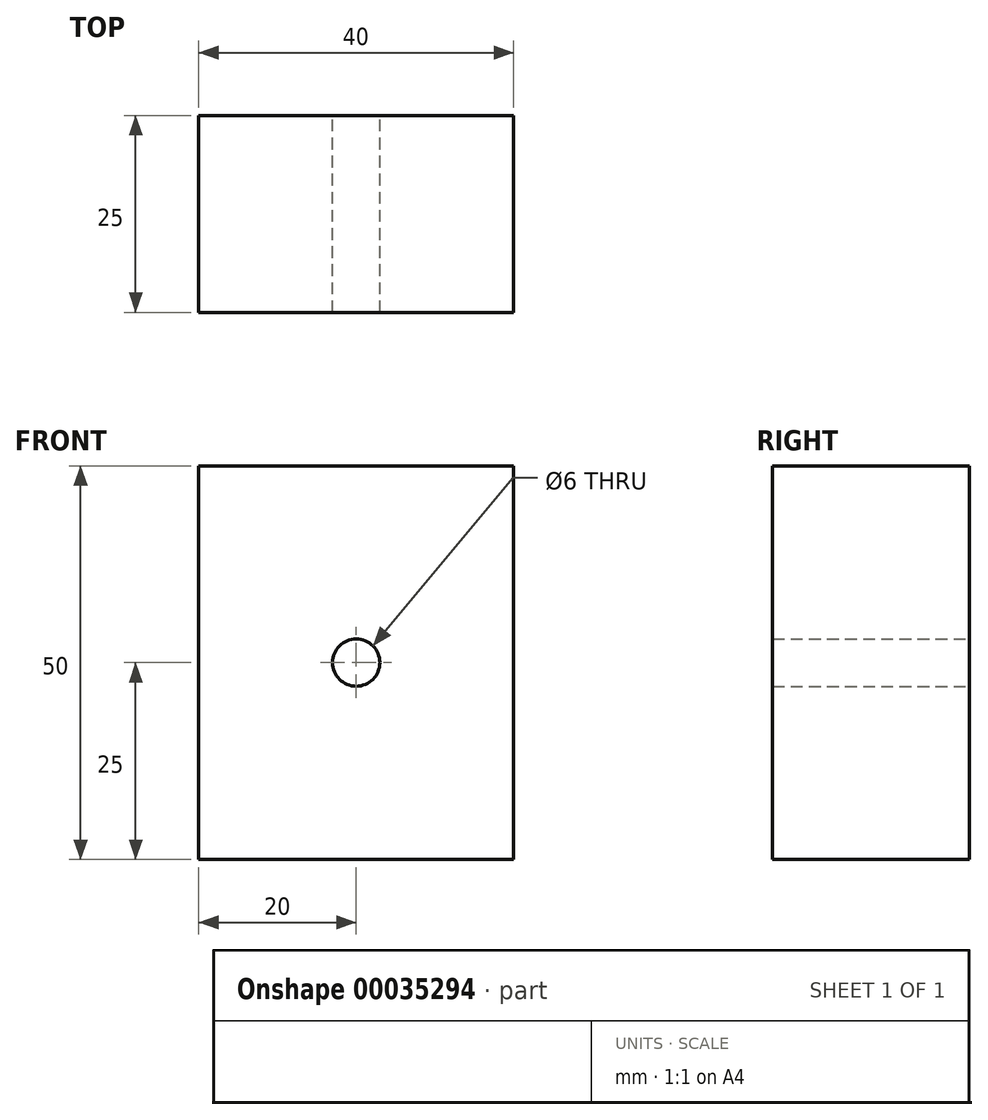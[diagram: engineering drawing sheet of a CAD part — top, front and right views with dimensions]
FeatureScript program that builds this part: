
annotation { "Feature Type Name" : "Feature", "Feature Type Description" : "" }
export const myFeature = defineFeature(function(context is Context, id is Id, definition is map)
    precondition{}
    {
        {
            var Q0;
            Q0=qCreatedBy(makeId("Front.planeOp"),FACE);
            var sketch = newSketch(context, id + "F0", { "sketchPlane" : qUnion([Q0])});
            skCircle(sketch, "E0", {"center": v(0, 0) * mm, "radius": 3 * mm});
            skLineSegment(sketch, "E1.bottom", {"start": v(-20, 25) * mm, "end": v(20, 25) * mm});
            skLineSegment(sketch, "E1.top", {"start": v(-20, -25) * mm, "end": v(20, -25) * mm});
            skLineSegment(sketch, "E1.left", {"start": v(-20, 25) * mm, "end": v(-20, -25) * mm});
            skLineSegment(sketch, "E1.right", {"start": v(20, 25) * mm, "end": v(20, -25) * mm});
            skSolve(sketch);
        }
        {
            var Q0;
            Q0 = qSketchRegion(id + "F0", true);
            extrude(context, id + "F1", {"entities" : qUnion([Q0]), "depth" : 25 * mm});
        }
    });
